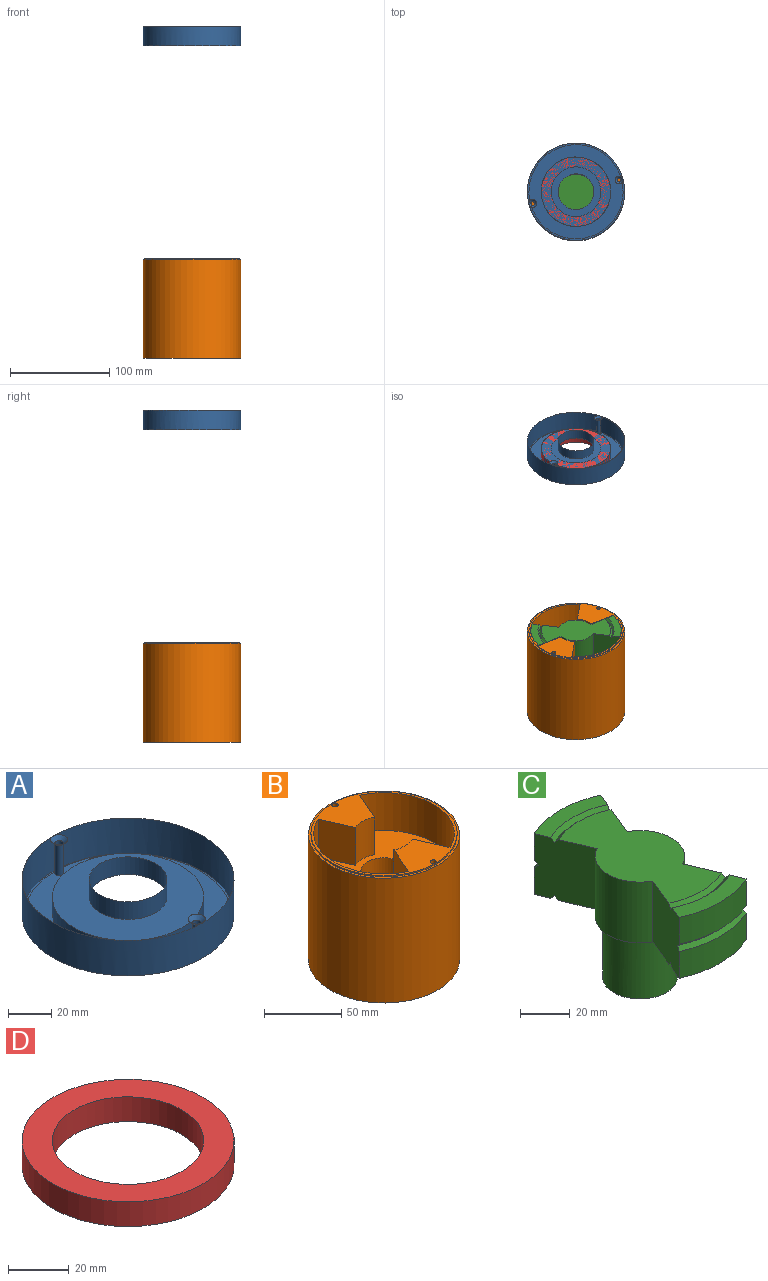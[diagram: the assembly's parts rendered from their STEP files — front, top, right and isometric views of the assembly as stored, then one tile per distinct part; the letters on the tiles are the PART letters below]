
ASSEMBLY  parts=4 mates=6
PART A: 12 faces, bbox 98x98x20 mm
  f0: cylinder r=2mm len=17mm, axis (0,0,-1), area 213.6mm2, adj f6,f10
  f1: cylinder r=49mm len=98mm, axis (0,0,-1), area 6157.5mm2, adj f3,f4
  f2: cylinder r=2mm len=17mm, axis (0,0,-1), area 213.6mm2, adj f6,f11
  f3: plane 98x98mm, normal (0,0,1), area 6424.6mm2, adj f1,f9,f10,f11
  f4: plane 98x98mm, normal (0,0,-1), area 484.6mm2, adj f1,f5
  f5: cylinder r=47.4mm len=94.8mm, axis (0,0,-1), area 297.8mm2, adj f4,f6
  f6: plane 94.8x94.8mm, normal (0,0,-1), area 3184.8mm2, adj f0,f2,f5,f7
  f7: cylinder r=35mm len=70mm, axis (0,0,-1), area 1979.2mm2, adj f6,f8
  f8: plane 70x70mm, normal (0,0,-1), area 2830.6mm2, adj f7,f9
  f9: cylinder r=18mm len=36mm, axis (0,0,-1), area 1131mm2, adj f3,f8
  f10: cone r=2mm half-angle=45deg, axis (0,0,1), area 53.3mm2, adj f0,f3
  f11: cone r=2mm half-angle=45deg, axis (0,0,1), area 53.3mm2, adj f2,f3
PART B: 27 faces, bbox 98x98x100 mm
  f0: cylinder r=49mm len=99mm, axis (0,0,1), area 30479.7mm2, adj f1,f3
  f1: plane 98x98mm, normal (0,0,-1), area 6958.4mm2, adj f0,f20,f21,f22,f23,f24,f25
  f2: cylinder r=47.4mm len=94.8mm, axis (0,0,1), area 297.8mm2, adj f3,f4
  f3: plane 98x98mm, normal (0,0,1), area 484.6mm2, adj f0,f2
  f4: plane 94.8x94.8mm, normal (0,0,1), area 1982.9mm2, adj f2,f5,f6,f7,f8,f9,f10,f11
  f5: cylinder r=19.5mm len=30mm, axis (0,0,1), area 527.7mm2, adj f4,f6,f12,f13
  f6: plane 30x23.9mm, normal (0.92,0.4,0), area 783.2mm2, adj f4,f5,f7,f13
  f7: cylinder r=45.6mm len=82.91mm, axis (0,0,1), area 3121.8mm2, adj f4,f6,f8,f13
  f8: plane 30x23.9mm, normal (0.92,-0.4,0), area 783.2mm2, adj f4,f7,f9,f13
  f9: cylinder r=19.5mm len=30mm, axis (0,0,1), area 527.7mm2, adj f4,f8,f10,f13
  f10: plane 30x23.9mm, normal (-0.92,-0.4,0), area 783.2mm2, adj f4,f9,f11,f13
  f11: cylinder r=45.6mm len=82.91mm, axis (0,0,1), area 3121.8mm2, adj f4,f10,f12,f13
  f12: plane 30x23.9mm, normal (-0.92,0.4,0), area 783.2mm2, adj f4,f5,f11,f13
  f13: plane 91.2x82.91mm, normal (0,0,1), area 4343.5mm2, adj f5,f6,f7,f8,f9,f10,f11,f12
  f14: cylinder r=15mm len=30mm, axis (0,0,1), area 2827.4mm2, adj f13,f15
  f15: plane 30x30mm, normal (0,0,1), area 706.9mm2, adj f14
  f16: cylinder r=2mm len=10mm, axis (0,0,1), area 125.7mm2, adj f4,f17
  f17: plane 4x4mm, normal (0,0,1), area 12.6mm2, adj f16
  f18: cylinder r=2mm len=10mm, axis (0,0,1), area 125.7mm2, adj f4,f19
  f19: plane 4x4mm, normal (0,0,1), area 12.6mm2, adj f18
  f20: plane 30x15mm, normal (-0.02,1,0), area 450mm2, adj f1,f21,f25,f26
  f21: plane 30x12.87mm, normal (0.86,0.51,0), area 450mm2, adj f1,f20,f22,f26
  f22: plane 30x13.11mm, normal (0.87,-0.49,0), area 450mm2, adj f1,f21,f23,f26
  f23: plane 30x15mm, normal (0.02,-1,0), area 450mm2, adj f1,f22,f24,f26
  f24: plane 30x12.87mm, normal (-0.86,-0.51,0), area 450mm2, adj f1,f23,f25,f26
  f25: plane 30x13.11mm, normal (-0.87,0.49,0), area 450mm2, adj f1,f20,f24,f26
  f26: plane 30x26.22mm, normal (0,0,-1), area 584.6mm2, adj f20,f21,f22,f23,f24,f25
PART C: 30 faces, bbox 38.1x91x59.7 mm
  f0: cylinder r=18mm len=31.73mm, axis (0,0,-1), area 1165.3mm2, adj f3,f6,f14,f18
  f1: cylinder r=18mm len=31.73mm, axis (0,0,-1), area 1165.3mm2, adj f2,f6,f14,f19
  f2: plane 30x25.48mm, normal (0.92,0.38,0), area 816.9mm2, adj f1,f6,f7,f8,f9,f10,f11,f12
  f3: plane 30x25.48mm, normal (-0.92,-0.38,0), area 816.9mm2, adj f0,f6,f14,f20,f21,f22,f23,f24
  f4: cylinder r=15mm len=30mm, axis (0,0,1), area 2799.2mm2, adj f5,f6
  f5: plane 30x30mm, normal (0,0,-1), area 706.9mm2, adj f4
  f6: plane 69.4x36mm, normal (0,0,-1), area 1120.3mm2, adj f0,f1,f2,f3,f4,f17,f18,f19
  f7: cylinder r=45.5mm len=38mm, axis (0,0,-1), area 517.5mm2, adj f2,f8,f16,f18
  f8: cone r=43.7mm half-angle=45deg, axis (0,0,-1), area 98mm2, adj f2,f7,f9,f18
  f9: cone r=45.5mm half-angle=45deg, axis (0,0,1), area 98mm2, adj f2,f8,f10,f18
  f10: cylinder r=45.5mm len=38mm, axis (0,0,-1), area 517.5mm2, adj f2,f9,f11,f18
  f11: plane 38x10.82mm, normal (0,0,1), area 262mm2, adj f2,f10,f12,f18
  f12: cone r=38.3mm half-angle=45deg, axis (0,0,1), area 83.7mm2, adj f2,f11,f13,f18
  f13: cone r=36.5mm half-angle=45deg, axis (0,0,-1), area 80.1mm2, adj f2,f12,f14,f18
  f14: plane 69.4x36mm, normal (0,0,1), area 1827.2mm2, adj f0,f1,f2,f3,f13,f18,f19,f27
  f15: cone r=38.3mm half-angle=45deg, axis (0,0,-1), area 83.7mm2, adj f2,f16,f17,f18
  f16: plane 38x10.82mm, normal (0,0,-1), area 262mm2, adj f2,f7,f15,f18
  f17: cone r=36.5mm half-angle=45deg, axis (0,0,1), area 80.1mm2, adj f2,f6,f15,f18
  f18: plane 30x25.48mm, normal (-0.92,0.38,0), area 816.9mm2, adj f0,f6,f7,f8,f9,f10,f11,f12
  f19: plane 30x25.48mm, normal (0.92,-0.38,0), area 816.9mm2, adj f1,f6,f14,f20,f21,f22,f23,f24
  f20: cylinder r=45.5mm len=38mm, axis (0,0,-1), area 517.5mm2, adj f3,f19,f21,f25
  f21: plane 38x10.82mm, normal (0,0,1), area 262mm2, adj f3,f19,f20,f26
  f22: plane 38x10.82mm, normal (0,0,-1), area 262mm2, adj f3,f19,f23,f28
  f23: cylinder r=45.5mm len=38mm, axis (0,0,-1), area 517.5mm2, adj f3,f19,f22,f24
  f24: cone r=43.7mm half-angle=45deg, axis (0,0,-1), area 98mm2, adj f3,f19,f23,f25
  f25: cone r=45.5mm half-angle=45deg, axis (0,0,1), area 98mm2, adj f3,f19,f20,f24
  f26: cone r=38.3mm half-angle=45deg, axis (0,0,1), area 83.7mm2, adj f3,f19,f21,f27
  f27: cone r=36.5mm half-angle=45deg, axis (0,0,-1), area 80.1mm2, adj f3,f14,f19,f26
  f28: cone r=38.3mm half-angle=45deg, axis (0,0,-1), area 83.7mm2, adj f3,f19,f22,f29
  f29: cone r=36.5mm half-angle=45deg, axis (0,0,1), area 80.1mm2, adj f3,f6,f19,f28
PART D: 4 faces, bbox 70x70x10 mm
  f0: cylinder r=25mm len=50mm, axis (0,0,-1), area 1570.8mm2, adj f2,f3
  f1: cylinder r=35mm len=70mm, axis (0,0,-1), area 2199.1mm2, adj f2,f3
  f2: plane 70x70mm, normal (0,0,1), area 1885mm2, adj f0,f1
  f3: plane 70x70mm, normal (0,0,-1), area 1885mm2, adj f0,f1
PLACE A rot(axis=(0,0,1),105.2deg) t=(18.21,8.12,214.18)mm
PLACE B rot(axis=(0,0,-1),74.8deg) t=(18.21,8.12,0)mm fixed
PLACE C rot(axis=(0,0,1),55.2deg) t=(18.21,8.12,-30)mm
PLACE D rot(axis=(0,0,1),15.2deg) t=(18.21,8.12,214.18)mm
MATE planar D.f1 <-> A.f5  axis (0,0,1) through (18.21,8.12,224.18)mm
MATE parallel A.f1 <-> B.f7  axis (0,0,-1) through (18.21,8.12,214.18)mm
MATE cylindrical A.f2 <-> B.f18  axis (0,0,1) through (61.64,19.88,232.18)mm
MATE cylindrical C.f4 <-> B.f14  axis (0,0,-1) through (18.21,8.12,-59.7)mm
MATE slider D.f0 <-> A.f9  axis (0,0,1) through (18.21,8.12,224.18)mm
MATE cylindrical A.f0 <-> B.f16  axis (0,0,1) through (-25.23,-3.65,234.18)mm
